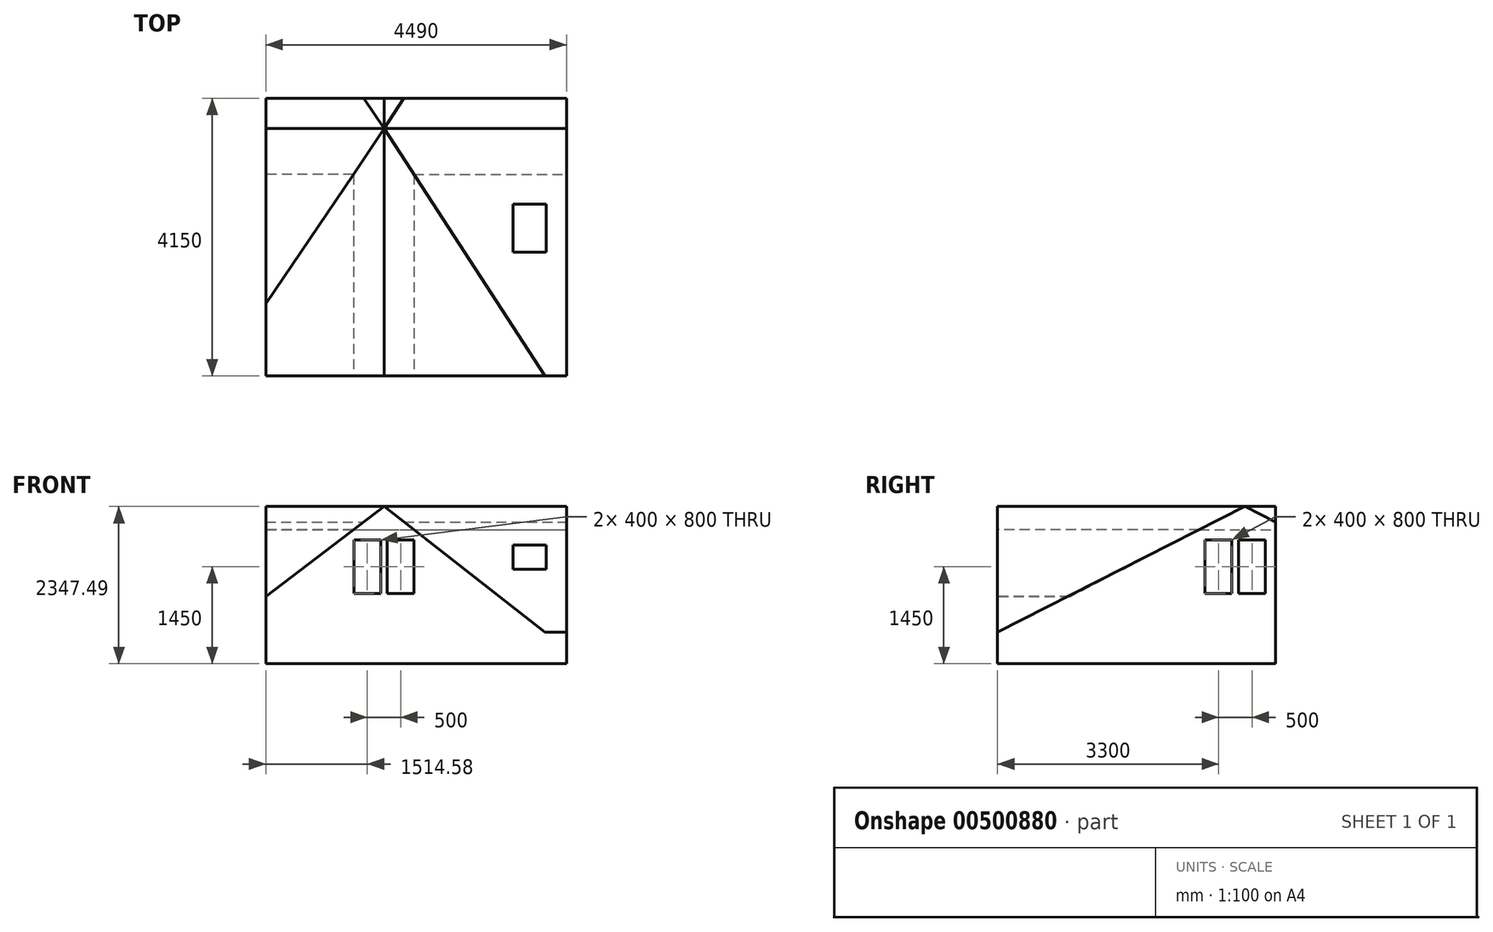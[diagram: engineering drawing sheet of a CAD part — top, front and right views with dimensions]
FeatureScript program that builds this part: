
annotation { "Feature Type Name" : "Feature", "Feature Type Description" : "" }
export const myFeature = defineFeature(function(context is Context, id is Id, definition is map)
    precondition{}
    {
        {
            var Q0;
            Q0=qCreatedBy(makeId("Top.planeOp"),FACE);
            var sketch = newSketch(context, id + "F0", { "sketchPlane" : qUnion([Q0])});
            skLineSegment(sketch, "E0.bottom", {"start": v(0, 0) * mm, "end": v(4490, 0) * mm});
            skLineSegment(sketch, "E0.top", {"start": v(0, 4150) * mm, "end": v(4490, 4150) * mm});
            skLineSegment(sketch, "E0.left", {"start": v(0, 0) * mm, "end": v(0, 4150) * mm});
            skLineSegment(sketch, "E0.right", {"start": v(4490, 0) * mm, "end": v(4490, 4150) * mm});
            skSolve(sketch);
        }
        {
            var Q0;
            Q0 = qSketchRegion(id + "F0", true);
            extrude(context, id + "F1", {"entities" : qUnion([Q0]), "depth" : 2000 * mm, "offsetDistance" : 25 * mm});
        }
        {
            var Q0;
            Q0=makeQuery(id+"F1.opExtrude","CAP_FACE",FACE,{"disambiguationData":[OSD([sQuery(id+"F0.wireOp",EDGE,"E0.bottom"),sQuery(id+"F0.wireOp",EDGE,"E0.top"),sQuery(id+"F0.wireOp",EDGE,"E0.left"),sQuery(id+"F0.wireOp",EDGE,"E0.right")])],"isStart":false});
            var sketch = newSketch(context, id + "F2", { "sketchPlane" : qUnion([Q0])});
            skLineSegment(sketch, "E1", {"start": v(0, 3010) * mm, "end": v(1310, 3010) * mm});
            skLineSegment(sketch, "E2", {"start": v(1310, 3010) * mm, "end": v(1310, 0) * mm});
            skLineSegment(sketch, "E3", {"start": v(2210, 0) * mm, "end": v(2210, 3010) * mm});
            skLineSegment(sketch, "E4", {"start": v(2210, 3010) * mm, "end": v(4490, 3010) * mm});
            skLineSegment(sketch, "E5", {"start": v(1310, 3010) * mm, "end": v(0, 1080) * mm});
            skLineSegment(sketch, "E6", {"start": v(3490, 0) * mm, "end": v(3490, 1040) * mm});
            skLineSegment(sketch, "E7", {"start": v(3490, 1040) * mm, "end": v(4490, 1040) * mm});
            skLineSegment(sketch, "E8", {"start": v(2210, 3010) * mm, "end": v(3490, 1040) * mm});
            skSolve(sketch);
        }
        {
            var Q0;
            Q0=sQuery(id+"F2.wireOp",EDGE,"E8");
            cPlane(context, id + "F3", {"entities" : qUnion([Q0]), "cplaneType" : CPlaneType.LINE_ANGLE, "offset" : 25 * mm, "angle" : 90 * degree, "width" : 150 * mm, "height" : 150 * mm});
        }
        {
            var Q0;
            Q0=sQuery(id+"F2.wireOp",EDGE,"E5");
            cPlane(context, id + "F4", {"entities" : qUnion([Q0]), "cplaneType" : CPlaneType.LINE_ANGLE, "offset" : 25 * mm, "angle" : 90 * degree, "width" : 150 * mm, "height" : 150 * mm});
        }
        {
            var Q0;
            Q0=makeQuery(id+"F1.opExtrude","SWEPT_FACE",FACE,{"disambiguationData":[OSD([sQuery(id+"F0.wireOp",EDGE,"E0.right")])]});
            var sketch = newSketch(context, id + "F5", { "sketchPlane" : qUnion([Q0])});
            skLineSegment(sketch, "E9", {"start": v(3010, 2000) * mm, "end": v(1040, 1000) * mm});
            skLineSegment(sketch, "E10", {"start": v(0, 1000) * mm, "end": v(0, 2000) * mm});
            skLineSegment(sketch, "E11", {"start": v(0, 2000) * mm, "end": v(3010, 2000) * mm});
            skLineSegment(sketch, "E12", {"start": v(1040, 1000) * mm, "end": v(0, 472.08) * mm});
            skLineSegment(sketch, "E13", {"start": v(0, 472.08) * mm, "end": v(0, 1000) * mm});
            skSolve(sketch);
        }
        {
            var Q0;
            Q0 = qSketchRegion(id + "F5", true);
            var Q1;
            Q1=qCreatedBy(id+"F3.planeOp",FACE);
            extrude(context, id + "F6", {"entities" : qUnion([Q0]), "operationType" : NewBodyOperationType.REMOVE, "endBound" : BoundingType.UP_TO_SURFACE, "oppositeDirection" : true, "depth" : 25 * mm, "endBoundEntityFace" : qUnion([Q1]), "offsetDistance" : 25 * mm});
        }
        {
            var Q0;
            Q0=makeQuery(id+"F1.opExtrude","SWEPT_FACE",FACE,{"disambiguationData":[OSD([sQuery(id+"F0.wireOp",EDGE,"E0.bottom")])]});
            var sketch = newSketch(context, id + "F7", { "sketchPlane" : qUnion([Q0])});
            skLineSegment(sketch, "E14", {"start": v(2210, 2000) * mm, "end": v(3490, 1000) * mm});
            skLineSegment(sketch, "E15", {"start": v(3490, 1000) * mm, "end": v(4165.74, 472.08) * mm});
            skLineSegment(sketch, "E16", {"start": v(4165.74, 472.08) * mm, "end": v(4165.74, 2000) * mm});
            skLineSegment(sketch, "E17", {"start": v(2210, 2000) * mm, "end": v(4165.74, 2000) * mm});
            skSolve(sketch);
        }
        {
            var Q0;
            Q0 = qSketchRegion(id + "F7", true);
            var Q1;
            Q1=qCreatedBy(id+"F3.planeOp",FACE);
            extrude(context, id + "F8", {"entities" : qUnion([Q0]), "operationType" : NewBodyOperationType.REMOVE, "endBound" : BoundingType.UP_TO_SURFACE, "oppositeDirection" : true, "depth" : 25 * mm, "endBoundEntityFace" : qUnion([Q1]), "offsetDistance" : 25 * mm});
        }
        {
            var Q0;
            Q0=makeQuery(id+"F1.opExtrude","SWEPT_FACE",FACE,{"disambiguationData":[OSD([sQuery(id+"F0.wireOp",EDGE,"E0.left")])]});
            var sketch = newSketch(context, id + "F9", { "sketchPlane" : qUnion([Q0])});
            skLineSegment(sketch, "E18", {"start": v(-3010, 2000) * mm, "end": v(-1080, 1000) * mm});
            skLineSegment(sketch, "E19", {"start": v(-1080, 1000) * mm, "end": v(0, 1000) * mm});
            skLineSegment(sketch, "E20", {"start": v(0, 1000) * mm, "end": v(0, 2000) * mm});
            skLineSegment(sketch, "E21", {"start": v(0, 2000) * mm, "end": v(-3010, 2000) * mm});
            skSolve(sketch);
        }
        {
            var Q0;
            Q0 = qSketchRegion(id + "F9", true);
            var Q1;
            Q1=qCreatedBy(id+"F4.planeOp",FACE);
            extrude(context, id + "F10", {"entities" : qUnion([Q0]), "operationType" : NewBodyOperationType.REMOVE, "endBound" : BoundingType.UP_TO_SURFACE, "oppositeDirection" : true, "depth" : 25 * mm, "endBoundEntityFace" : qUnion([Q1]), "offsetDistance" : 25 * mm});
        }
        {
            var Q0;
            Q0=makeQuery(id+"F1.opExtrude","SWEPT_FACE",FACE,{"disambiguationData":[OSD([sQuery(id+"F0.wireOp",EDGE,"E0.bottom")])]});
            var sketch = newSketch(context, id + "F11", { "sketchPlane" : qUnion([Q0])});
            skLineSegment(sketch, "E22", {"start": v(1310, 2000) * mm, "end": v(0, 1000) * mm});
            skLineSegment(sketch, "E23", {"start": v(0, 1000) * mm, "end": v(0, 2000) * mm});
            skLineSegment(sketch, "E24", {"start": v(0, 2000) * mm, "end": v(1310, 2000) * mm});
            skSolve(sketch);
        }
        {
            var Q0;
            Q0 = qSketchRegion(id + "F11", true);
            var Q1;
            Q1=qCreatedBy(id+"F4.planeOp",FACE);
            extrude(context, id + "F12", {"entities" : qUnion([Q0]), "operationType" : NewBodyOperationType.REMOVE, "endBound" : BoundingType.UP_TO_SURFACE, "oppositeDirection" : true, "depth" : 25 * mm, "endBoundEntityFace" : qUnion([Q1]), "offsetDistance" : 25 * mm});
        }
        {
            var Q0;
            Q0=makeQuery(id+"F1.opExtrude","CAP_FACE",FACE,{"disambiguationData":[OSD([sQuery(id+"F0.wireOp",EDGE,"E0.bottom"),sQuery(id+"F0.wireOp",EDGE,"E0.top"),sQuery(id+"F0.wireOp",EDGE,"E0.left"),sQuery(id+"F0.wireOp",EDGE,"E0.right")])],"isStart":true});
            shell(context, id + "F13", {"entities" : qUnion([Q0]), "thickness" : 2.5 * mm});
        }
        {
            var Q0;
            Q0=makeQuery(id+"F1.opExtrude","SWEPT_FACE",FACE,{"disambiguationData":[OSD([sQuery(id+"F0.wireOp",EDGE,"E0.bottom")])]});
            var sketch = newSketch(context, id + "F14", { "sketchPlane" : qUnion([Q0])});
            skLineSegment(sketch, "E25.bottom", {"start": v(1314.58, 1850) * mm, "end": v(1714.58, 1850) * mm});
            skLineSegment(sketch, "E25.top", {"start": v(1314.58, 1050) * mm, "end": v(1714.58, 1050) * mm});
            skLineSegment(sketch, "E25.left", {"start": v(1314.58, 1850) * mm, "end": v(1314.58, 1050) * mm});
            skLineSegment(sketch, "E25.right", {"start": v(1714.58, 1850) * mm, "end": v(1714.58, 1050) * mm});
            skLineSegment(sketch, "E26.bottom", {"start": v(1814.58, 1850) * mm, "end": v(2214.58, 1850) * mm});
            skLineSegment(sketch, "E26.top", {"start": v(1814.58, 1050) * mm, "end": v(2214.58, 1050) * mm});
            skLineSegment(sketch, "E26.left", {"start": v(1814.58, 1850) * mm, "end": v(1814.58, 1050) * mm});
            skLineSegment(sketch, "E26.right", {"start": v(2214.58, 1850) * mm, "end": v(2214.58, 1050) * mm});
            skSolve(sketch);
        }
        {
            var Q0;
            Q0 = qSketchRegion(id + "F14", true);
            extrude(context, id + "F15", {"entities" : qUnion([Q0]), "operationType" : NewBodyOperationType.REMOVE, "endBound" : BoundingType.UP_TO_NEXT, "oppositeDirection" : true, "depth" : 25 * mm, "offsetDistance" : 25 * mm});
        }
        {
            var Q0;
            Q0=makeQuery(id+"F1.opExtrude","SWEPT_FACE",FACE,{"disambiguationData":[OSD([sQuery(id+"F0.wireOp",EDGE,"E0.right")])]});
            var sketch = newSketch(context, id + "F16", { "sketchPlane" : qUnion([Q0])});
            skLineSegment(sketch, "E27.bottom", {"start": v(4000, 1850) * mm, "end": v(3600, 1850) * mm});
            skLineSegment(sketch, "E27.top", {"start": v(4000, 1050) * mm, "end": v(3600, 1050) * mm});
            skLineSegment(sketch, "E27.left", {"start": v(4000, 1850) * mm, "end": v(4000, 1050) * mm});
            skLineSegment(sketch, "E27.right", {"start": v(3600, 1850) * mm, "end": v(3600, 1050) * mm});
            skLineSegment(sketch, "E28.bottom", {"start": v(3500, 1850) * mm, "end": v(3100, 1850) * mm});
            skLineSegment(sketch, "E28.top", {"start": v(3500, 1050) * mm, "end": v(3100, 1050) * mm});
            skLineSegment(sketch, "E28.left", {"start": v(3500, 1850) * mm, "end": v(3500, 1050) * mm});
            skLineSegment(sketch, "E28.right", {"start": v(3100, 1850) * mm, "end": v(3100, 1050) * mm});
            skSolve(sketch);
        }
        {
            var Q0;
            Q0 = qSketchRegion(id + "F16", true);
            extrude(context, id + "F17", {"entities" : qUnion([Q0]), "operationType" : NewBodyOperationType.REMOVE, "endBound" : BoundingType.UP_TO_NEXT, "oppositeDirection" : true, "depth" : 25 * mm, "offsetDistance" : 25 * mm});
        }
        {
            var Q0;
            Q0=makeQuery(id+"F6.boolean.opBoolean","COPY",FACE,{"derivedFrom":makeQuery(id+"F6.opExtrude","SWEPT_FACE",FACE,{"disambiguationData":[OSD([sQuery(id+"F5.wireOp",EDGE,"E9"),sQuery(id+"F5.wireOp",EDGE,"E12")])]})});
            var sketch = newSketch(context, id + "F18", { "sketchPlane" : qUnion([Q0])});
            skLineSegment(sketch, "E29.bottom", {"start": v(4190, 3089.28) * mm, "end": v(3690, 3089.28) * mm});
            skLineSegment(sketch, "E29.top", {"start": v(4190, 2289.28) * mm, "end": v(3690, 2289.28) * mm});
            skLineSegment(sketch, "E29.left", {"start": v(4190, 3089.28) * mm, "end": v(4190, 2289.28) * mm});
            skLineSegment(sketch, "E29.right", {"start": v(3690, 3089.28) * mm, "end": v(3690, 2289.28) * mm});
            skSolve(sketch);
        }
        {
            var Q0;
            Q0 = qSketchRegion(id + "F18", true);
            extrude(context, id + "F19", {"entities" : qUnion([Q0]), "operationType" : NewBodyOperationType.REMOVE, "endBound" : BoundingType.UP_TO_NEXT, "oppositeDirection" : true, "depth" : 25 * mm, "offsetDistance" : 25 * mm});
        }
        {
            var Q0;
            Q0=makeQuery(id+"F1.opExtrude","SWEPT_FACE",FACE,{"disambiguationData":[OSD([sQuery(id+"F0.wireOp",EDGE,"E0.bottom")])]});
            var sketch = newSketch(context, id + "F20", { "sketchPlane" : qUnion([Q0])});
            skLineSegment(sketch, "E30", {"start": v(1310, 2000) * mm, "end": v(1765.21, 2347.5) * mm});
            skLineSegment(sketch, "E31", {"start": v(1765.21, 2347.5) * mm, "end": v(2210, 2000) * mm});
            skLineSegment(sketch, "E32", {"start": v(2210, 2000) * mm, "end": v(1310, 2000) * mm});
            skSolve(sketch);
        }
        {
            var Q0;
            Q0 = qSketchRegion(id + "F20", true);
            var Q1;
            Q1=makeQuery(id+"F1.opExtrude","SWEPT_FACE",FACE,{"disambiguationData":[OSD([sQuery(id+"F0.wireOp",EDGE,"E0.top")])]});
            extrude(context, id + "F21", {"entities" : qUnion([Q0]), "operationType" : NewBodyOperationType.ADD, "endBound" : BoundingType.UP_TO_SURFACE, "oppositeDirection" : true, "depth" : 25 * mm, "endBoundEntityFace" : qUnion([Q1]), "offsetDistance" : 25 * mm});
        }
        {
            var Q0;
            Q0=makeQuery(id+"F1.opExtrude","SWEPT_FACE",FACE,{"disambiguationData":[OSD([sQuery(id+"F0.wireOp",EDGE,"E0.right")])]});
            var sketch = newSketch(context, id + "F22", { "sketchPlane" : qUnion([Q0])});
            skLineSegment(sketch, "E33", {"start": v(3010, 2000) * mm, "end": v(3694.56, 2347.5) * mm});
            skLineSegment(sketch, "E34", {"start": v(3694.56, 2347.5) * mm, "end": v(4150, 2116.3) * mm});
            skLineSegment(sketch, "E35", {"start": v(4150, 2116.3) * mm, "end": v(4150, 2000) * mm});
            skLineSegment(sketch, "E36", {"start": v(4150, 2000) * mm, "end": v(3010, 2000) * mm});
            skSolve(sketch);
        }
        {
            var Q0;
            Q0 = qSketchRegion(id + "F22", true);
            var Q1;
            Q1=makeQuery(id+"F1.opExtrude","SWEPT_FACE",FACE,{"disambiguationData":[OSD([sQuery(id+"F0.wireOp",EDGE,"E0.left")])]});
            extrude(context, id + "F23", {"entities" : qUnion([Q0]), "operationType" : NewBodyOperationType.ADD, "endBound" : BoundingType.UP_TO_SURFACE, "oppositeDirection" : true, "depth" : 25 * mm, "endBoundEntityFace" : qUnion([Q1]), "offsetDistance" : 25 * mm});
        }
    });
